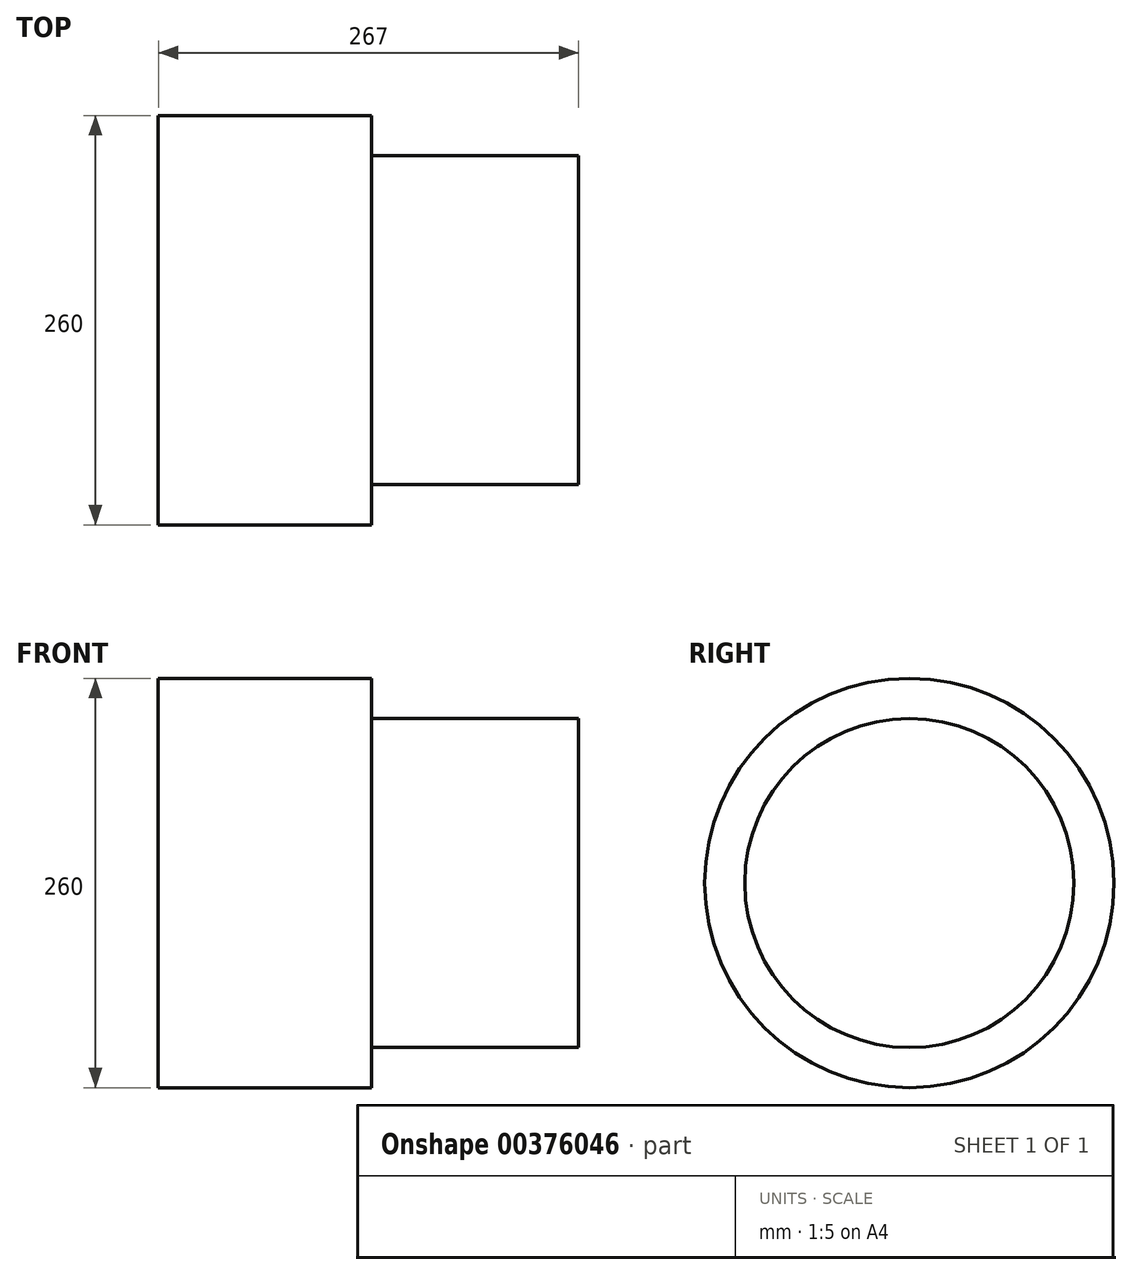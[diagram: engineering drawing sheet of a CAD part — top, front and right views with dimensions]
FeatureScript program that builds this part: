
annotation { "Feature Type Name" : "Feature", "Feature Type Description" : "" }
export const myFeature = defineFeature(function(context is Context, id is Id, definition is map)
    precondition{}
    {
        {
            var Q0;
            Q0=qCreatedBy(makeId("Front.planeOp"),FACE);
            var sketch = newSketch(context, id + "F0", { "sketchPlane" : qUnion([Q0])});
            skLineSegment(sketch, "E0", {"start": v(296.17, 0) * mm, "end": v(-312.05, 0) * mm, "construction": true});
            skLineSegment(sketch, "E1", {"start": v(-88.81, 0) * mm, "end": v(-88.81, 130) * mm});
            skLineSegment(sketch, "E2", {"start": v(-88.81, 130) * mm, "end": v(46.69, 130) * mm});
            skLineSegment(sketch, "E3", {"start": v(46.69, 130) * mm, "end": v(46.69, 104.5) * mm});
            skLineSegment(sketch, "E4", {"start": v(46.69, 104.5) * mm, "end": v(178.19, 104.5) * mm});
            skLineSegment(sketch, "E5", {"start": v(178.19, 104.5) * mm, "end": v(178.19, 0) * mm});
            skLineSegment(sketch, "E6", {"start": v(162.19, 0) * mm, "end": v(-88.81, 0) * mm});
            skLineSegment(sketch, "E7.MirrorCS", {"start": v(-88.81, 0) * mm, "end": v(-88.81, -130) * mm});
            skLineSegment(sketch, "E8.MirrorCS", {"start": v(-88.81, -130) * mm, "end": v(46.69, -130) * mm});
            skLineSegment(sketch, "E9.MirrorCS", {"start": v(46.69, -130) * mm, "end": v(46.69, -104.5) * mm});
            skLineSegment(sketch, "E10.MirrorCS", {"start": v(46.69, -104.5) * mm, "end": v(178.19, -104.5) * mm});
            skLineSegment(sketch, "E11.MirrorCS", {"start": v(178.19, -104.5) * mm, "end": v(178.19, 0) * mm});
            skLineSegment(sketch, "E12", {"start": v(-88.81, 0) * mm, "end": v(178.19, 0) * mm});
            skLineSegment(sketch, "E13", {"start": v(162.19, 0) * mm, "end": v(22.12, 0) * mm});
            skSolve(sketch);
        }
        {
            var Q0;
            Q0=makeQuery(id+"F0.imprint","IMPRINT",FACE,{"disambiguationData":[TD([[makeQuery(id+"F0.imprint","IMPRINT",EDGE,{"derivedFrom":sQuery(id+"F0.wireOp",EDGE,"E1")}),-1.0]])]});
            var Q1;
            Q1=sQuery(id+"F0.wireOp",EDGE,"E0");
            revolve(context, id + "F1", {"entities" : qUnion([Q0]), "axis" : qUnion([Q1]), "revolveType" : RevolveType.FULL, "oppositeDirection" : true});
        }
    });
